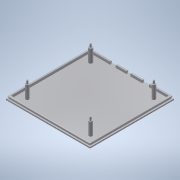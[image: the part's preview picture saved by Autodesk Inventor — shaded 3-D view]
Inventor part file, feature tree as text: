
AUTODESK INVENTOR PART (.ipt)
format: ipt  version: 2022.3 (Build 263350000, 350)  size: 242,688 bytes
history: native  units: mm
features: other x9, extrude x6, reference x4, pattern_circular x1, projected_geometry x1, sketch x1
ambient origin geometry x8: Origin, YZ Plane, XZ Plane, XY Plane, X Axis, Y Axis, Z Axis, Center Point
bodies: Solid1 (feature_tree)
feature tree (22):
  extrude  "Bottom"  TaperAngle=0.0deg  [1 undecoded]
  extrude  "Walls"  TaperAngle=90.0deg  [1 undecoded]
  other  "Lip_front_profile"
  extrude  "Lip_front"  TaperAngle=180.0deg  [1 undecoded]
  other  "Lip_corner"
  pattern_circular  "Lip_mirroring"  [2 undecoded]
  extrude  "PCB_post_inner"  Depth=4.0mm TaperAngle=0.0deg
  extrude  "PCB_post_outer"  TaperAngle=90.0deg  [1 undecoded]
  extrude  "Extrusion7"  Depth=4.0mm TaperAngle=360.0deg
  other  "Bottom_profile"
  other  "Wall_profile"
  projected_geometry  "Projected Loop1"
  other  "PCB_mounting_holes"
  reference  "Reference1"
  reference  "Reference2"
  reference  "Reference3"
  reference  "Reference4"
  other  "PCB_post_outer_offsets"
  sketch  "Sketch8"  dims[d2=2.0mm d3=0.0mm d7=0.0mm d9=90.0deg d10=180.0deg d11=1.0mm d12=8.5mm d13=0.0mm d20=90.0deg d21=40.0mm d22=360.0deg d24=25.0mm d25=-0.174533mm d26=1.0mm d27=1.0mm d29=1.0mm d30=1.0mm d31=20.0mm d32=0.0mm d33=4.0mm d34=0.0mm d35=0.5mm d36=0.872665mm]
  other  "<userpath>\Dropbox (Personal)\SuperSTEM\FIB\FIBcontroller\Enclosure\Enclosure_with_PCB.iam"
  other  "Enclosure_with_PCB.iam"
  other  "FIBcontroller:1"
note: 6 required parameter values undecoded (feature->parameter linkage not recoverable at this tier; creation-order binding heuristic only, values carry confidence <= 0.55)
